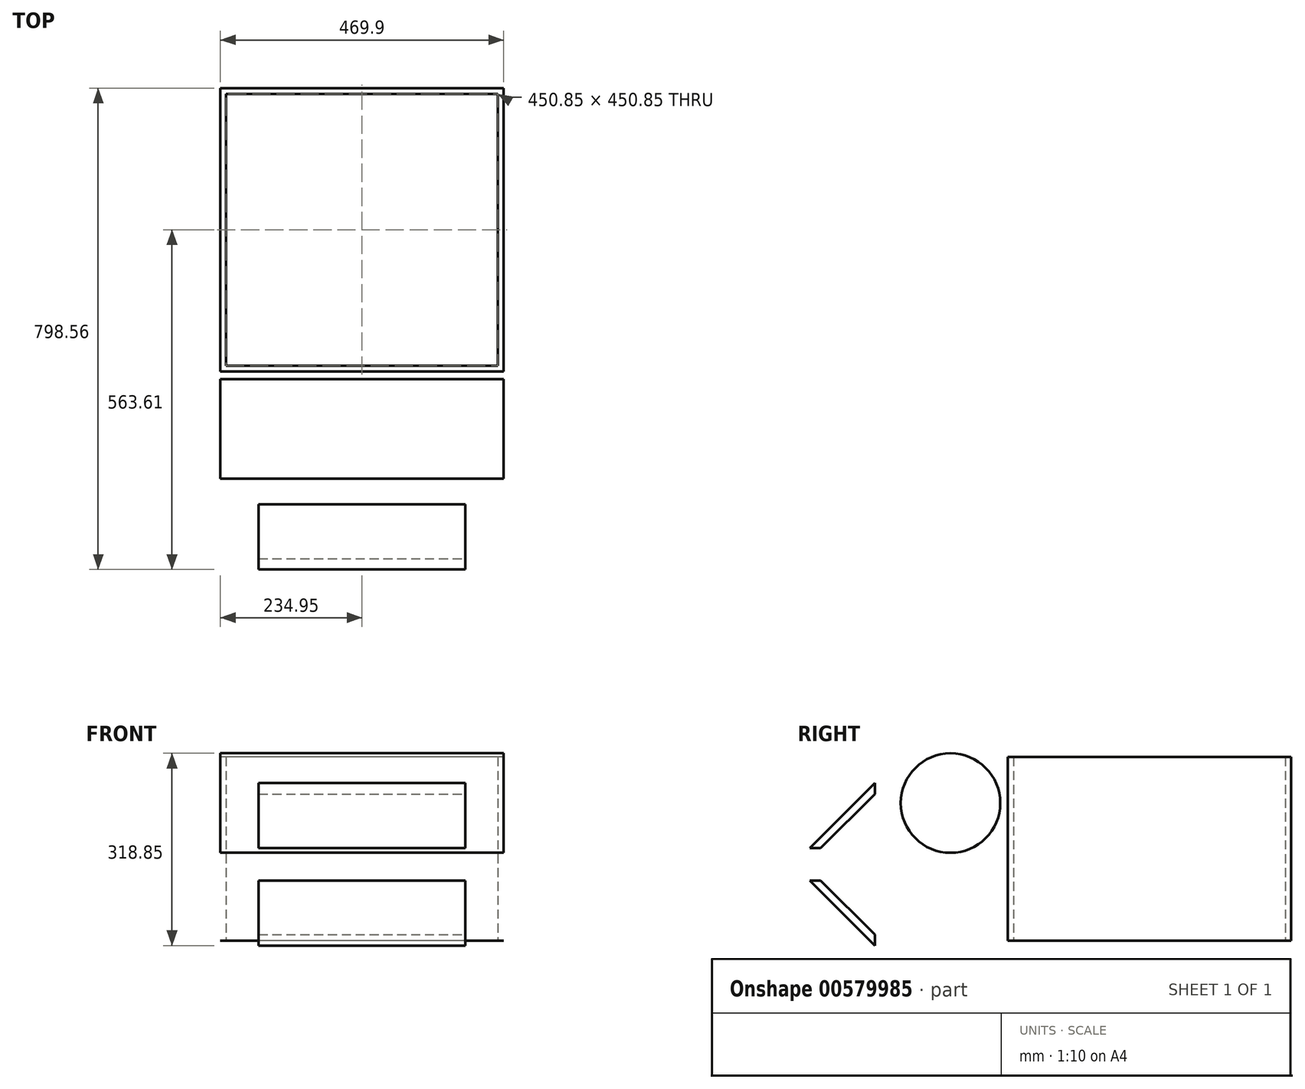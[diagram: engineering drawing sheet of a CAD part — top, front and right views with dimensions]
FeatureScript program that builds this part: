
annotation { "Feature Type Name" : "Feature", "Feature Type Description" : "" }
export const myFeature = defineFeature(function(context is Context, id is Id, definition is map)
    precondition{}
    {
        {
            var Q0;
            Q0=qCreatedBy(makeId("Top.planeOp"),FACE);
            var sketch = newSketch(context, id + "F0", { "sketchPlane" : qUnion([Q0])});
            skLineSegment(sketch, "E0.bottom", {"start": v(234.95, -234.95) * mm, "end": v(-234.95, -234.95) * mm});
            skLineSegment(sketch, "E0.top", {"start": v(234.95, 234.95) * mm, "end": v(-234.95, 234.95) * mm});
            skLineSegment(sketch, "E0.left", {"start": v(234.95, -234.95) * mm, "end": v(234.95, 234.95) * mm});
            skLineSegment(sketch, "E0.right", {"start": v(-234.95, -234.95) * mm, "end": v(-234.95, 234.95) * mm});
            skPoint(sketch, "E0.middle", {"position": v(0, 0) * mm});
            skLineSegment(sketch, "E1.0", {"start": v(-225.43, -225.43) * mm, "end": v(-225.43, 225.43) * mm});
            skLineSegment(sketch, "E1.1", {"start": v(225.42, -225.42) * mm, "end": v(-225.43, -225.43) * mm});
            skLineSegment(sketch, "E1.2", {"start": v(225.42, -225.43) * mm, "end": v(225.43, 225.43) * mm});
            skLineSegment(sketch, "E1.3", {"start": v(225.43, 225.43) * mm, "end": v(-225.43, 225.43) * mm});
            skSolve(sketch);
        }
        {
            var Q0;
            Q0=qSketchRegion(id+"F0",true);
            extrude(context, id + "F1", {"entities" : qUnion([Q0]), "depth" : 304.8 * mm, "offsetDistance" : 25.4 * mm});
        }
        {
            var Q0;
            Q0=makeQuery(id+"F1.opExtrude","SWEPT_FACE",FACE,{"disambiguationData":[OSD([sQuery(id+"F0.wireOp",EDGE,"E0.left")])]});
            var sketch = newSketch(context, id + "F2", { "sketchPlane" : qUnion([Q0])});
            skLineSegment(sketch, "E2", {"start": v(-234.95, 0) * mm, "end": v(-234.95, 228.6) * mm});
            skLineSegment(sketch, "E3", {"start": v(-234.95, 228.6) * mm, "end": v(-330.2, 228.6) * mm});
            skCircle(sketch, "E4", {"center": v(-330.2, 228.6) * mm, "radius": 82.55 * mm});
            skSolve(sketch);
        }
        {
            var Q0;
            Q0=qSketchRegion(id+"F2",true);
            extrude(context, id + "F3", {"entities" : qUnion([Q0]), "oppositeDirection" : true, "depth" : 469.9 * mm, "offsetDistance" : 25.4 * mm});
        }
        {
            var Q0;
            Q0=makeQuery(id+"F1.opExtrude","SWEPT_FACE",FACE,{"disambiguationData":[OSD([sQuery(id+"F0.wireOp",EDGE,"E0.left")])]});
            var sketch = newSketch(context, id + "F4", { "sketchPlane" : qUnion([Q0])});
            skLineSegment(sketch, "E5", {"start": v(-234.95, 0) * mm, "end": v(-234.95, 127) * mm});
            skLineSegment(sketch, "E6", {"start": v(-234.95, 127) * mm, "end": v(-590.55, 127) * mm});
            skLineSegment(sketch, "E7", {"start": v(-590.55, 127) * mm, "end": v(-455.85, 261.7) * mm});
            skLineSegment(sketch, "E8.MirrorCS", {"start": v(-590.55, 127) * mm, "end": v(-455.85, -7.7) * mm});
            skLineSegment(sketch, "E9", {"start": v(-590.55, 127) * mm, "end": v(-563.6, 153.94) * mm});
            skLineSegment(sketch, "E10.MirrorCS", {"start": v(-590.55, 127) * mm, "end": v(-563.6, 100.06) * mm});
            skLineSegment(sketch, "E11", {"start": v(-563.6, 153.94) * mm, "end": v(-509.73, 207.82) * mm});
            skLineSegment(sketch, "E12", {"start": v(-509.73, 207.82) * mm, "end": v(-500.75, 198.84) * mm});
            skLineSegment(sketch, "E13", {"start": v(-455.85, 261.7) * mm, "end": v(-455.85, 243.74) * mm});
            skLineSegment(sketch, "E14", {"start": v(-500.75, 198.84) * mm, "end": v(-455.85, 243.74) * mm});
            skLineSegment(sketch, "E15.MirrorCS", {"start": v(-500.75, 198.84) * mm, "end": v(-545.65, 153.94) * mm});
            skLineSegment(sketch, "E16.MirrorCS", {"start": v(-563.6, 153.94) * mm, "end": v(-545.65, 153.94) * mm});
            skLineSegment(sketch, "E17.MirrorCS", {"start": v(-563.6, 100.06) * mm, "end": v(-545.65, 100.06) * mm});
            skLineSegment(sketch, "E18.MirrorCS", {"start": v(-500.75, 55.16) * mm, "end": v(-545.65, 100.06) * mm});
            skLineSegment(sketch, "E19.MirrorCS", {"start": v(-500.75, 55.16) * mm, "end": v(-455.85, 10.26) * mm});
            skLineSegment(sketch, "E20.MirrorCS", {"start": v(-563.6, 100.06) * mm, "end": v(-509.73, 46.18) * mm});
            skLineSegment(sketch, "E21.MirrorCS", {"start": v(-455.85, -7.7) * mm, "end": v(-455.85, 10.26) * mm});
            skLineSegment(sketch, "E22.MirrorCS", {"start": v(-509.73, 46.18) * mm, "end": v(-500.75, 55.16) * mm});
            skSolve(sketch);
        }
        {
            var Q0;
            Q0=qSketchRegion(id+"F4",true);
            extrude(context, id + "F5", {"entities" : qUnion([Q0]), "oppositeDirection" : true, "depth" : 406.4 * mm, "offsetDistance" : 25.4 * mm, "hasSecondDirection" : true, "secondDirectionOppositeDirection" : true, "secondDirectionDepth" : 63.5 * mm});
        }
    });
